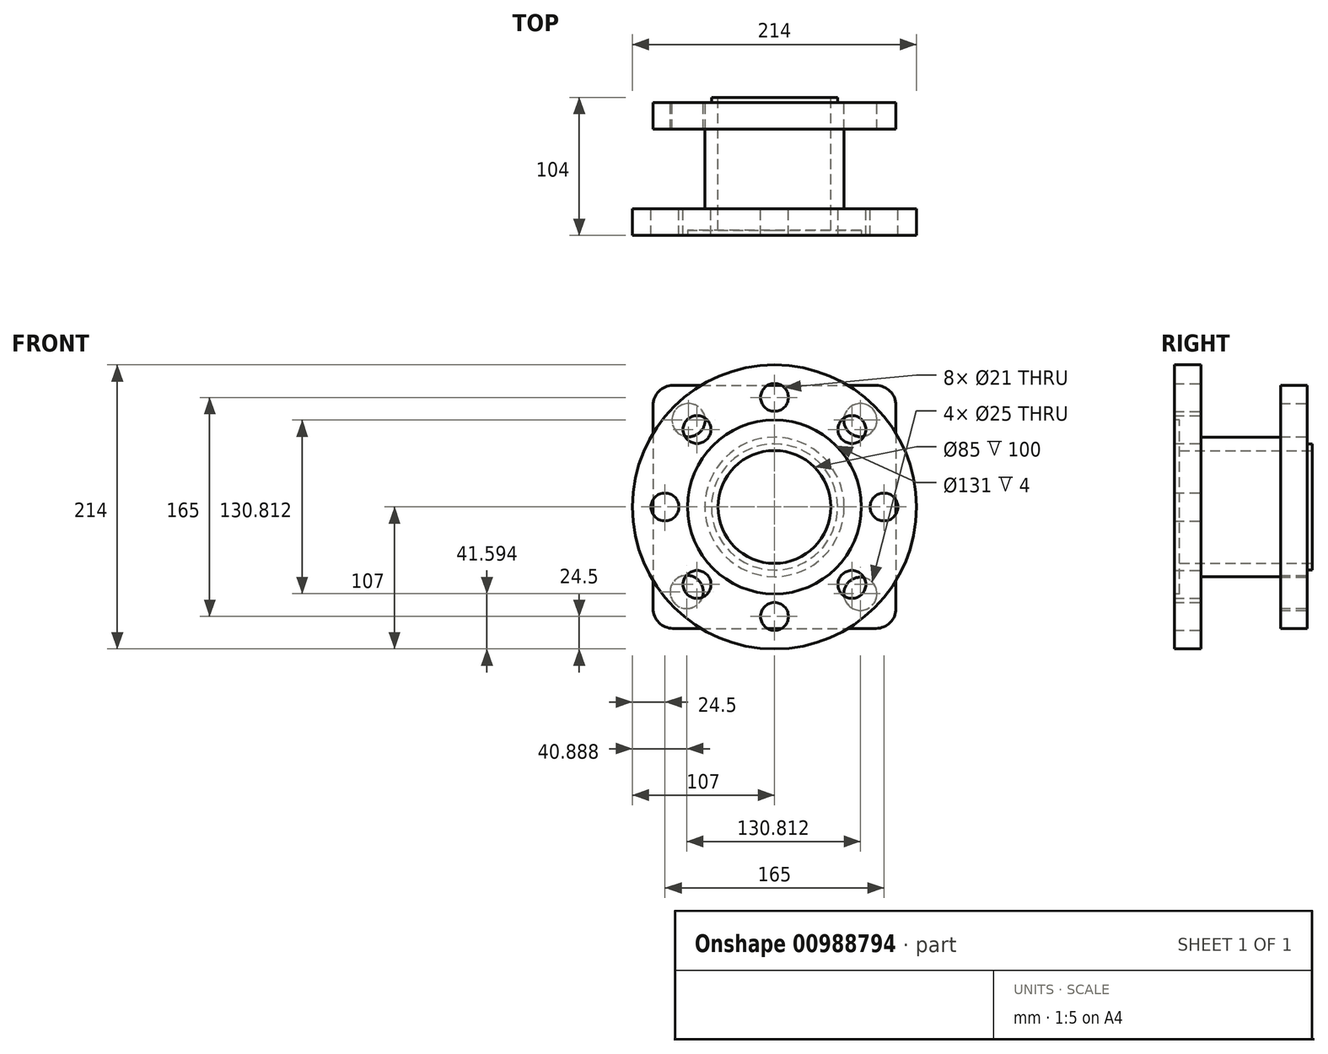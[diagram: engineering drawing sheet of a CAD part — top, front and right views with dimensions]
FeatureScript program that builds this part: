
annotation { "Feature Type Name" : "Feature", "Feature Type Description" : "" }
export const myFeature = defineFeature(function(context is Context, id is Id, definition is map)
    precondition{}
    {
        {
            var Q0;
            Q0=qCreatedBy(makeId("Front.planeOp"),FACE);
            var sketch = newSketch(context, id + "F0", { "sketchPlane" : qUnion([Q0])});
            skLineSegment(sketch, "E0.bottom", {"start": v(-91.5, 91.5) * mm, "end": v(91.5, 91.5) * mm});
            skLineSegment(sketch, "E0.top", {"start": v(-91.5, -91.5) * mm, "end": v(91.5, -91.5) * mm});
            skLineSegment(sketch, "E0.left", {"start": v(-91.5, 91.5) * mm, "end": v(-91.5, -91.5) * mm});
            skLineSegment(sketch, "E0.right", {"start": v(91.5, 91.5) * mm, "end": v(91.5, -91.5) * mm});
            skPoint(sketch, "E0.middle", {"position": v(0, 0) * mm});
            skCircle(sketch, "E1", {"center": v(0, 0) * mm, "radius": 42.5 * mm});
            skPoint(sketch, "E2", {"position": v(64.7, 65.4) * mm});
            skPoint(sketch, "E3.1.0", {"position": v(-64.7, 65.4) * mm});
            skPoint(sketch, "E3.2.0", {"position": v(-66.11, -64) * mm});
            skPoint(sketch, "E3.3.0", {"position": v(64.7, -65.4) * mm});
            skSolve(sketch);
        }
        {
            var Q0;
            Q0=makeQuery(id+"F0.imprint","IMPRINT",FACE,{"disambiguationData":[TD([[makeQuery(id+"F0.imprint","IMPRINT",EDGE,{"derivedFrom":sQuery(id+"F0.wireOp",EDGE,"E0.bottom")}),-1.0]])]});
            extrude(context, id + "F1", {"entities" : qUnion([Q0]), "depth" : 20 * mm, "offsetDistance" : 25 * mm});
        }
        {
            var Q0;
            Q0=makeQuery(id+"F1.opExtrude","SWEPT_EDGE",EDGE,{"disambiguationData":[OSD([sQuery(id+"F0.wireOp",EDGE,"E0.bottom"),sQuery(id+"F0.wireOp",EDGE,"E0.left")])]});
            var Q1;
            Q1=makeQuery(id+"F1.opExtrude","SWEPT_EDGE",EDGE,{"disambiguationData":[OSD([sQuery(id+"F0.wireOp",EDGE,"E0.bottom"),sQuery(id+"F0.wireOp",EDGE,"E0.right")])]});
            var Q2;
            Q2=makeQuery(id+"F1.opExtrude","SWEPT_EDGE",EDGE,{"disambiguationData":[OSD([sQuery(id+"F0.wireOp",EDGE,"E0.top"),sQuery(id+"F0.wireOp",EDGE,"E0.right")])]});
            var Q3;
            Q3=makeQuery(id+"F1.opExtrude","SWEPT_EDGE",EDGE,{"disambiguationData":[OSD([sQuery(id+"F0.wireOp",EDGE,"E0.top"),sQuery(id+"F0.wireOp",EDGE,"E0.left")])]});
            fillet(context, id + "F2", {"entities" : qUnion([Q0, Q1, Q2, Q3]), "radius" : 15 * mm, "tangentPropagation" : true, "allowEdgeOverflow" : false});
        }
        {
            var Q0;
            Q0=sQuery(id+"F0.wireOp",VERTEX,"E3.3.0");
            var Q1;
            Q1=sQuery(id+"F0.wireOp",VERTEX,"E2");
            var Q2;
            Q2=sQuery(id+"F0.wireOp",VERTEX,"E3.1.0");
            var Q3;
            Q3=sQuery(id+"F0.wireOp",VERTEX,"E3.2.0");
            var Q4;
            Q4=makeQuery(id+"F1.opExtrude","SWEPT_BODY",BODY,{"disambiguationData":[OSD([sQuery(id+"F0.wireOp",EDGE,"E0.bottom"),sQuery(id+"F0.wireOp",EDGE,"E0.top"),sQuery(id+"F0.wireOp",EDGE,"E0.left"),sQuery(id+"F0.wireOp",EDGE,"E0.right"),sQuery(id+"F0.wireOp",EDGE,"E1")])]});
            hole(context, id + "F3", {"style" : HoleStyle.SIMPLE, "endStyle" : HoleEndStyle.BLIND, "oppositeDirection" : true, "standardTappedOrClearance" : lookupTablePath({ "standard" : "ISO", "engagement" : "75%", "pitch" : "2 mm", "size" : "M27", "type" : "Tapped" }), "standardBlindInLast" : lookupTablePath({ "standard" : "ISO", "fit" : "Normal", "engagement" : "75%", "pitch" : "2 mm", "size" : "M27", "type" : "Clearance & tapped" }), "holeDiameter" : 25 * mm, "majorDiameter" : 27 * mm, "showTappedDepth" : true, "holeDepth" : 31 * mm, "isTappedThrough" : true, "tappedDepth" : 25 * mm, "tapClearance" : 3, "locations" : qUnion([Q0, Q1, Q2, Q3]), "scope" : qUnion([Q4])});
        }
        {
            var Q0;
            Q0=makeQuery(id+"F0.imprint","IMPRINT",FACE,{"disambiguationData":[TD([[makeQuery(id+"F0.imprint","IMPRINT",EDGE,{"derivedFrom":sQuery(id+"F0.wireOp",EDGE,"E0.bottom")}),-1.0]])]});
            var sketch = newSketch(context, id + "F4", { "sketchPlane" : qUnion([Q0])});
            skCircle(sketch, "E4", {"center": v(0, 0) * mm, "radius": 47.5 * mm});
            skSolve(sketch);
        }
        {
            var Q0;
            Q0=makeQuery(id+"F4.imprint","IMPRINT",FACE,{"disambiguationData":[TD([[makeQuery(id+"F4.imprint","IMPRINT",EDGE,{"derivedFrom":sQuery(id+"F4.wireOp",EDGE,"E4")}),1.0]])]});
            extrude(context, id + "F5", {"entities" : qUnion([Q0]), "operationType" : NewBodyOperationType.ADD, "oppositeDirection" : true, "depth" : 4 * mm, "offsetDistance" : 25 * mm});
        }
        {
            var Q0;
            Q0=makeQuery(id+"F1.opExtrude","CAP_FACE",FACE,{"disambiguationData":[OSD([sQuery(id+"F0.wireOp",EDGE,"E0.bottom"),sQuery(id+"F0.wireOp",EDGE,"E0.top"),sQuery(id+"F0.wireOp",EDGE,"E0.left"),sQuery(id+"F0.wireOp",EDGE,"E0.right"),sQuery(id+"F0.wireOp",EDGE,"E1")])],"isStart":false});
            var sketch = newSketch(context, id + "F6", { "sketchPlane" : qUnion([Q0])});
            skCircle(sketch, "E5", {"center": v(0, 0) * mm, "radius": 52.5 * mm});
            skCircle(sketch, "E6", {"center": v(0, 0) * mm, "radius": 42.5 * mm});
            skSolve(sketch);
        }
        {
            var Q0;
            Q0 = qSketchRegion(id + "F6", true);
            extrude(context, id + "F7", {"entities" : qUnion([Q0]), "operationType" : NewBodyOperationType.ADD, "depth" : 60 * mm, "offsetDistance" : 25 * mm});
        }
        {
            var Q0;
            Q0=makeQuery(id+"F7.opExtrude","CAP_FACE",FACE,{"disambiguationData":[OSD([sQuery(id+"F6.wireOp",EDGE,"E5"),sQuery(id+"F6.wireOp",EDGE,"E6")])],"isStart":false});
            var sketch = newSketch(context, id + "F8", { "sketchPlane" : qUnion([Q0])});
            skCircle(sketch, "E7", {"center": v(0, 0) * mm, "radius": 107 * mm});
            skPoint(sketch, "E8", {"position": v(58.34, -58.34) * mm});
            skPoint(sketch, "E9.1.0", {"position": v(82.5, 0) * mm});
            skPoint(sketch, "E9.2.0", {"position": v(58.34, 58.34) * mm});
            skPoint(sketch, "E9.3.0", {"position": v(0, 82.5) * mm});
            skPoint(sketch, "E9.4.0", {"position": v(-58.34, 58.34) * mm});
            skPoint(sketch, "E9.5.0", {"position": v(-82.5, 0) * mm});
            skPoint(sketch, "E9.6.0", {"position": v(-58.34, -58.34) * mm});
            skPoint(sketch, "E9.7.0", {"position": v(0, -82.5) * mm});
            skCircle(sketch, "E10", {"center": v(0, 0) * mm, "radius": 42.5 * mm});
            skSolve(sketch);
        }
        {
            var Q0;
            Q0 = qSketchRegion(id + "F8", true);
            extrude(context, id + "F9", {"entities" : qUnion([Q0]), "operationType" : NewBodyOperationType.ADD, "depth" : 20 * mm, "offsetDistance" : 25 * mm});
        }
        {
            var Q0;
            Q0=sQuery(id+"F8.wireOp",VERTEX,"E9.1.0");
            var Q1;
            Q1=sQuery(id+"F8.wireOp",VERTEX,"E9.2.0");
            var Q2;
            Q2=sQuery(id+"F8.wireOp",VERTEX,"E9.3.0");
            var Q3;
            Q3=sQuery(id+"F8.wireOp",VERTEX,"E9.4.0");
            var Q4;
            Q4=sQuery(id+"F8.wireOp",VERTEX,"E9.5.0");
            var Q5;
            Q5=sQuery(id+"F8.wireOp",VERTEX,"E9.6.0");
            var Q6;
            Q6=sQuery(id+"F8.wireOp",VERTEX,"E9.7.0");
            var Q7;
            Q7=sQuery(id+"F8.wireOp",VERTEX,"E8");
            var Q8;
            Q8=makeQuery(id+"F1.opExtrude","SWEPT_BODY",BODY,{"disambiguationData":[OSD([sQuery(id+"F0.wireOp",EDGE,"E0.bottom"),sQuery(id+"F0.wireOp",EDGE,"E0.top"),sQuery(id+"F0.wireOp",EDGE,"E0.left"),sQuery(id+"F0.wireOp",EDGE,"E0.right"),sQuery(id+"F0.wireOp",EDGE,"E1")])]});
            hole(context, id + "F10", {"style" : HoleStyle.SIMPLE, "endStyle" : HoleEndStyle.BLIND, "oppositeDirection" : true, "holeDiameter" : 21 * mm, "majorDiameter" : 20 * mm, "holeDepth" : 20 * mm, "isTappedThrough" : true, "tappedDepth" : 14 * mm, "tapClearance" : 0, "locations" : qUnion([Q0, Q1, Q2, Q3, Q4, Q5, Q6, Q7]), "scope" : qUnion([Q8])});
        }
        {
            var Q0;
            Q0=makeQuery(id+"F9.opExtrude","CAP_FACE",FACE,{"disambiguationData":[OSD([sQuery(id+"F8.wireOp",EDGE,"E7"),sQuery(id+"F8.wireOp",EDGE,"E10")])],"isStart":false});
            var sketch = newSketch(context, id + "F11", { "sketchPlane" : qUnion([Q0])});
            skCircle(sketch, "E11", {"center": v(0, 0) * mm, "radius": 65.5 * mm});
            skSolve(sketch);
        }
        {
            var Q0;
            Q0 = qSketchRegion(id + "F11", true);
            extrude(context, id + "F12", {"entities" : qUnion([Q0]), "operationType" : NewBodyOperationType.REMOVE, "oppositeDirection" : true, "depth" : 4 * mm, "offsetDistance" : 25 * mm});
        }
    });
